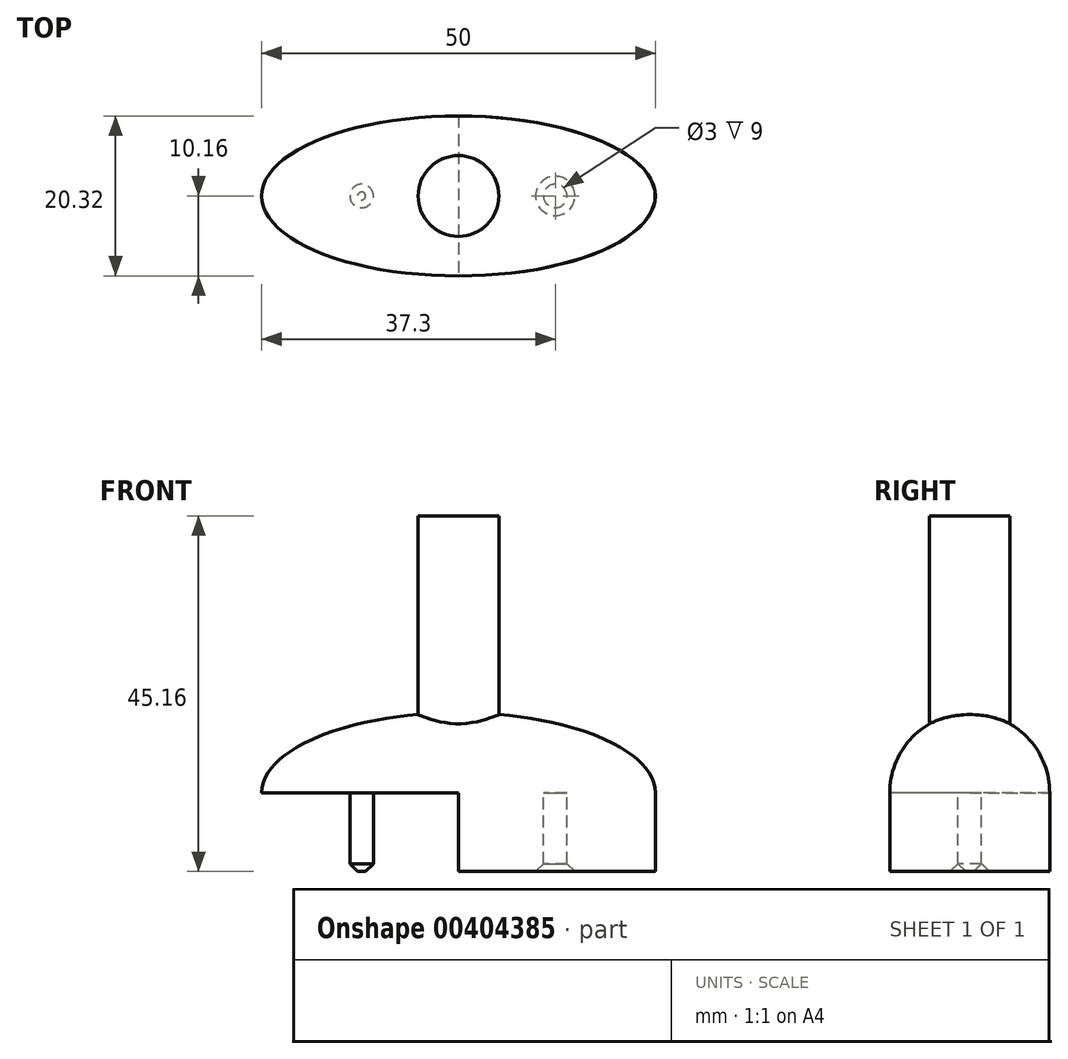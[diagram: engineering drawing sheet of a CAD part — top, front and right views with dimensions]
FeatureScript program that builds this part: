
annotation { "Feature Type Name" : "Feature", "Feature Type Description" : "" }
export const myFeature = defineFeature(function(context is Context, id is Id, definition is map)
    precondition{}
    {
        {
            assignVariable(context, id + "F0", {"name" : "W", "anyValue" : 20.32 * mm});
        }
        {
            var Q0;
            Q0=qCreatedBy(makeId("Top.planeOp"),FACE);
            var sketch = newSketch(context, id + "F1", { "sketchPlane" : qUnion([Q0])});
            skEllipticalArc(sketch, "E0", {});
            skLineSegment(sketch, "E1", {"start": v(-40, 0) * mm, "end": v(40, 0) * mm});
            const initialGuessF1  = {"E0": [0, 0, 1, 0, 0.025, 0.01016, 3.141592653589793, 0]};
            skSetInitialGuess(sketch, initialGuessF1);
            skSolve(sketch);
        }
        {
            var Q0;
            Q0=makeQuery(id+"F1.imprint","IMPRINT",FACE,{"disambiguationData":[TD([[makeQuery(id+"F1.imprint","IMPRINT",EDGE,{"derivedFrom":sQuery(id+"F1.wireOp",EDGE,"E0")}),1.0]])]});
            var Q1;
            Q1=sQuery(id+"F1.wireOp",EDGE,"E1");
            revolve(context, id + "F2", {"entities" : qUnion([Q0]), "axis" : qUnion([Q1]), "revolveType" : RevolveType.ONE_DIRECTION, "oppositeDirection" : true, "angle" : 180 * degree});
        }
        {
            var Q0;
            Q0=makeQuery(id+"F2.opRevolve","CAP_FACE",FACE,{"disambiguationData":[OSD([sQuery(id+"F1.wireOp",EDGE,"E0"),sQuery(id+"F1.wireOp",EDGE,"E1")])],"isStart":false});
            var sketch = newSketch(context, id + "F3", { "sketchPlane" : qUnion([Q0])});
            skEllipticalArc(sketch, "E2.0.0", {});
            skEllipticalArc(sketch, "E2.0.1", {});
            skCircle(sketch, "E3", {"center": v(-12.3, 0) * mm, "radius": 1.5 * mm});
            skLineSegment(sketch, "E4", {"start": v(0, -10.16) * mm, "end": v(0, 10.16) * mm});
            skCircle(sketch, "E5.MirrorC", {"center": v(12.3, 0) * mm, "radius": 1.5 * mm});
            const initialGuessF3  = {"E2.0.0": [0, 0, 1, 0, 0.025, 0.0125, 3.141592653589793, 0], "E2.0.1": [0, 0, 1, 0, 0.025, 0.0125, 0, 3.141592653589793]};
            skSetInitialGuess(sketch, initialGuessF3);
            skSolve(sketch);
        }
        {
            var Q0;
            Q0=makeQuery(id+"F3.imprint","IMPRINT",FACE,{"disambiguationData":[TD([[makeQuery(id+"F3.imprint","IMPRINT",EDGE,{"derivedFrom":sQuery(id+"F3.wireOp",EDGE,"E5.MirrorC")}),-1.0]])]});
            var Q1;
            Q1=makeQuery(id+"F3.imprint","IMPRINT",FACE,{"disambiguationData":[TD([[makeQuery(id+"F3.imprint","IMPRINT",EDGE,{"derivedFrom":sQuery(id+"F3.wireOp",EDGE,"E3")}),1.0]])]});
            extrude(context, id + "F4", {"entities" : qUnion([Q0, Q1]), "operationType" : NewBodyOperationType.ADD, "depth" : 10 * mm});
        }
        {
            var Q0;
            Q0=makeQuery(id+"F4.opExtrude","CAP_EDGE",EDGE,{"disambiguationData":[OSD([sQuery(id+"F3.wireOp",EDGE,"E5.MirrorC")])],"isStart":false});
            var Q1;
            Q1=makeQuery(id+"F4.opExtrude","CAP_EDGE",EDGE,{"disambiguationData":[OSD([sQuery(id+"F3.wireOp",EDGE,"E3")])],"isStart":false});
            chamfer(context, id + "F5", {"entities" : qUnion([Q0, Q1]), "width" : 1 * mm, "tangentPropagation" : true});
        }
        {
            var Q0;
            Q0=qCreatedBy(makeId("Top.planeOp"),FACE);
            cPlane(context, id + "F6", {"entities" : qUnion([Q0]), "cplaneType" : CPlaneType.OFFSET, "offset" : getVariable(context, 'W') / 2, "width" : 152.4 * mm, "height" : 152.4 * mm});
        }
        {
            var Q0;
            Q0=qCreatedBy(id+"F6.planeOp",FACE);
            var sketch = newSketch(context, id + "F7", { "sketchPlane" : qUnion([Q0])});
            skCircle(sketch, "E6", {"center": v(0, 0) * mm, "radius": 5.13 * mm});
            skSolve(sketch);
        }
        {
            var Q0;
            Q0=makeQuery(id+"F7.imprint","IMPRINT",FACE,{"disambiguationData":[TD([[makeQuery(id+"F7.imprint","IMPRINT",EDGE,{"derivedFrom":sQuery(id+"F7.wireOp",EDGE,"E6")}),1.0]])]});
            var Q1;
            Q1=makeQuery(id+"F2.opRevolve","SWEPT_FACE",FACE,{"disambiguationData":[OSD([sQuery(id+"F1.wireOp",EDGE,"E0")])]});
            extrude(context, id + "F8", {"entities" : qUnion([Q0]), "operationType" : NewBodyOperationType.ADD, "endBound" : BoundingType.UP_TO_SURFACE, "oppositeDirection" : true, "endBoundEntityFace" : qUnion([Q1]), "depth" : 26.16 * mm});
        }
        {
            var Q0;
            Q0=makeQuery(id+"F8.opExtrude","CAP_FACE",FACE,{"disambiguationData":[OSD([sQuery(id+"F7.wireOp",EDGE,"E6")])],"isStart":true});
            extrude(context, id + "F9", {"entities" : qUnion([Q0]), "operationType" : NewBodyOperationType.ADD, "depth" : 25 * mm});
        }
    });
